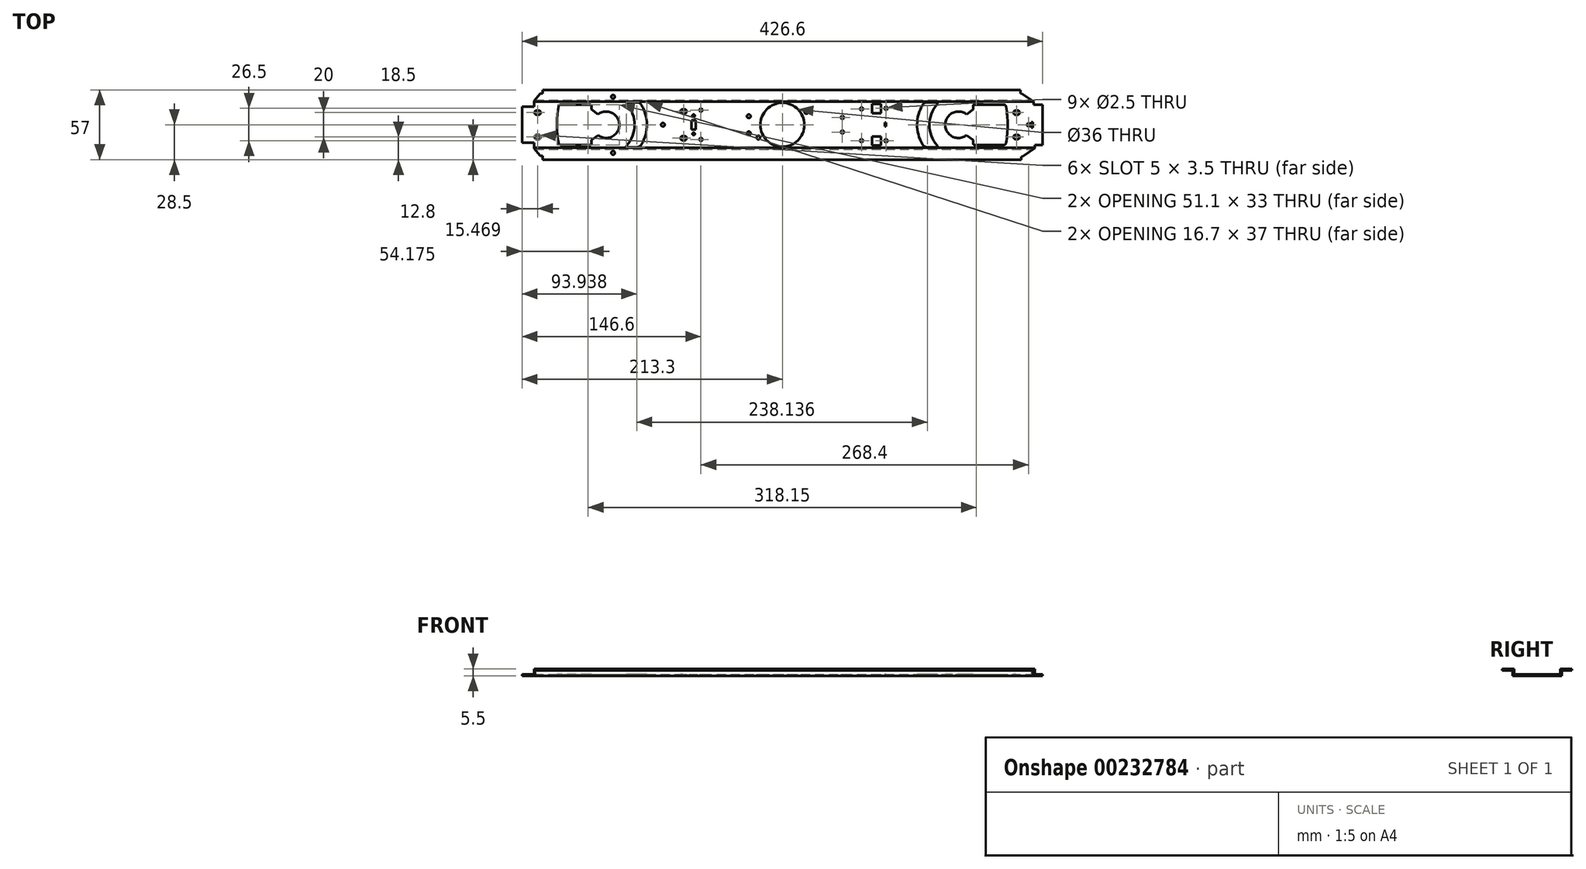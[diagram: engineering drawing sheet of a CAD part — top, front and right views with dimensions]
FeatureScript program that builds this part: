
annotation { "Feature Type Name" : "Feature", "Feature Type Description" : "" }
export const myFeature = defineFeature(function(context is Context, id is Id, definition is map)
    precondition{}
    {
        {
            var Q0;
            Q0=qCreatedBy(makeId("Top.planeOp"),FACE);
            var sketch = newSketch(context, id + "F0", { "sketchPlane" : qUnion([Q0])});
            skLineSegment(sketch, "E0.bottom", {"start": v(193, 29.4) * mm, "end": v(-197, 29.4) * mm});
            skLineSegment(sketch, "E0.top", {"start": v(193, -29.1) * mm, "end": v(-197, -29.1) * mm});
            skLineSegment(sketch, "E0.left", {"start": v(193, 29.4) * mm, "end": v(193, 26.65) * mm});
            skLineSegment(sketch, "E0.right", {"start": v(-197, 29.4) * mm, "end": v(-197, 26.8) * mm});
            skLineSegment(sketch, "E1.bottom", {"start": v(204, 19) * mm, "end": v(-204, 19) * mm, "construction": true});
            skLineSegment(sketch, "E1.top", {"start": v(204, -19) * mm, "end": v(-204, -19) * mm, "construction": true});
            skLineSegment(sketch, "E1.left", {"start": v(204, 19) * mm, "end": v(204, 17.25) * mm});
            skLineSegment(sketch, "E1.right", {"start": v(-204, 19) * mm, "end": v(-204, 15.75) * mm});
            skPoint(sketch, "E1.middle", {"position": v(0, 0) * mm});
            skPoint(sketch, "E2", {"position": v(193, 26.65) * mm});
            skPoint(sketch, "E3", {"position": v(194.1, 26.65) * mm});
            skLineSegment(sketch, "E4", {"start": v(194.1, 26.65) * mm, "end": v(204, 19) * mm});
            skLineSegment(sketch, "E5", {"start": v(194.1, 26.65) * mm, "end": v(193, 26.65) * mm});
            skLineSegment(sketch, "E6.MirrorCS", {"start": v(194.1, -26.65) * mm, "end": v(204, -19) * mm});
            skLineSegment(sketch, "E7.MirrorCS", {"start": v(194.1, -26.65) * mm, "end": v(193, -26.65) * mm});
            skPoint(sketch, "E8", {"position": v(-197, 26.8) * mm});
            skPoint(sketch, "E9", {"position": v(-199, 26.8) * mm});
            skLineSegment(sketch, "E10", {"start": v(-199, 26.8) * mm, "end": v(-204, 19) * mm});
            skLineSegment(sketch, "E11", {"start": v(-199, 26.8) * mm, "end": v(-197, 26.8) * mm});
            skLineSegment(sketch, "E12.MirrorCS", {"start": v(-199, -26.8) * mm, "end": v(-197, -26.8) * mm});
            skLineSegment(sketch, "E13.MirrorCS", {"start": v(-199, -26.8) * mm, "end": v(-204, -19) * mm});
            skPoint(sketch, "E14", {"position": v(-204, 0) * mm});
            skLineSegment(sketch, "E15", {"start": v(210.5, 0) * mm, "end": v(-236.37, 0) * mm, "construction": true});
            skPoint(sketch, "E16", {"position": v(-204, 29.4) * mm});
            skLineSegment(sketch, "E17", {"start": v(-204, -15.75) * mm, "end": v(-204, -19) * mm});
            skLineSegment(sketch, "E18", {"start": v(-204, 15.75) * mm, "end": v(-214.3, 15.75) * mm});
            skLineSegment(sketch, "E19", {"start": v(-214.3, 15.75) * mm, "end": v(-214.3, -15.75) * mm});
            skLineSegment(sketch, "E20", {"start": v(-214.3, -15.75) * mm, "end": v(-204, -15.75) * mm});
            skLineSegment(sketch, "E21", {"start": v(204, 17.25) * mm, "end": v(204, -17.25) * mm, "construction": true});
            skLineSegment(sketch, "E22", {"start": v(204, -17.25) * mm, "end": v(204, -19) * mm});
            skLineSegment(sketch, "E23", {"start": v(204, 17.25) * mm, "end": v(210.5, 17.25) * mm});
            skLineSegment(sketch, "E24", {"start": v(210.5, 17.25) * mm, "end": v(210.5, -17.25) * mm});
            skLineSegment(sketch, "E25", {"start": v(210.5, -17.25) * mm, "end": v(204, -17.25) * mm});
            skLineSegment(sketch, "E26", {"start": v(-197, 26.8) * mm, "end": v(-197, -26.8) * mm, "construction": true});
            skLineSegment(sketch, "E27", {"start": v(-197, -26.8) * mm, "end": v(-197, -29.1) * mm});
            skLineSegment(sketch, "E28", {"start": v(193, -26.65) * mm, "end": v(193, -29.1) * mm});
            skLineSegment(sketch, "E29", {"start": v(193, 26.65) * mm, "end": v(193, -26.65) * mm, "construction": true});
            skSolve(sketch);
        }
        {
            var Q0;
            Q0=qCreatedBy(makeId("Right.planeOp"),FACE);
            var sketch = newSketch(context, id + "F1", { "sketchPlane" : qUnion([Q0])});
            skLineSegment(sketch, "E30", {"start": v(0, 0) * mm, "end": v(20.1, 0) * mm});
            skPoint(sketch, "E31", {"position": v(20.1, 0) * mm});
            skLineSegment(sketch, "E32", {"start": v(20.1, 0) * mm, "end": v(20.1, 4.25) * mm});
            skPoint(sketch, "E33", {"position": v(29.4, 0) * mm});
            skLineSegment(sketch, "E34", {"start": v(20.1, 4.25) * mm, "end": v(29.4, 4.25) * mm});
            skLineSegment(sketch, "E35.0", {"start": v(18.85, 5.5) * mm, "end": v(29.4, 5.5) * mm});
            skLineSegment(sketch, "E35.1", {"start": v(18.85, 1.25) * mm, "end": v(18.85, 5.5) * mm});
            skLineSegment(sketch, "E35.2", {"start": v(0, 1.25) * mm, "end": v(18.85, 1.25) * mm});
            skLineSegment(sketch, "E36", {"start": v(29.4, 5.5) * mm, "end": v(29.4, 4.25) * mm});
            skLineSegment(sketch, "E37.MirrorCS", {"start": v(-29.4, 5.5) * mm, "end": v(-29.4, 4.25) * mm});
            skLineSegment(sketch, "E38.MirrorCS", {"start": v(0, 0) * mm, "end": v(-20.1, 0) * mm});
            skLineSegment(sketch, "E39.MirrorCS", {"start": v(0, 1.25) * mm, "end": v(-18.85, 1.25) * mm});
            skLineSegment(sketch, "E40.MirrorCS", {"start": v(-18.85, 1.25) * mm, "end": v(-18.85, 5.5) * mm});
            skLineSegment(sketch, "E41.MirrorCS", {"start": v(-20.1, 0) * mm, "end": v(-20.1, 4.25) * mm});
            skLineSegment(sketch, "E42.MirrorCS", {"start": v(-18.85, 5.5) * mm, "end": v(-29.4, 5.5) * mm});
            skLineSegment(sketch, "E43.MirrorCS", {"start": v(-20.1, 4.25) * mm, "end": v(-29.4, 4.25) * mm});
            skSolve(sketch);
        }
        {
            var Q0;
            Q0=makeQuery(id+"F1.imprint","IMPRINT",FACE,{"disambiguationData":[TD([[makeQuery(id+"F1.imprint","IMPRINT",EDGE,{"derivedFrom":sQuery(id+"F1.wireOp",EDGE,"E30")}),1.0]])]});
            extrude(context, id + "F2", {"entities" : qUnion([Q0]), "oppositeDirection" : true, "depth" : 213.75 * mm, "hasSecondDirection" : true, "secondDirectionOppositeDirection" : false, "secondDirectionDepth" : 213.3 * mm});
        }
        {
            var Q0;
            Q0=qCreatedBy(makeId("Top.planeOp"),FACE);
            var sketch = newSketch(context, id + "F3", { "sketchPlane" : qUnion([Q0])});
            skCircle(sketch, "E44", {"center": v(-27.5, 7) * mm, "radius": 1.5 * mm});
            skCircle(sketch, "E45", {"center": v(-66.7, 12) * mm, "radius": 1.25 * mm});
            skCircle(sketch, "E46", {"center": v(-97.9, 0) * mm, "radius": 1.5 * mm});
            skCircle(sketch, "E47", {"center": v(-72.7, 7.5) * mm, "radius": 1 * mm});
            skPoint(sketch, "E48", {"position": v(-200.5, 10) * mm});
            skLineSegment(sketch, "E49.bottom", {"start": v(-199.75, 11.75) * mm, "end": v(-201.25, 11.75) * mm});
            skLineSegment(sketch, "E49.top", {"start": v(-199.75, 8.25) * mm, "end": v(-201.25, 8.25) * mm});
            skLineSegment(sketch, "E49.left", {"start": v(-196.26, 9.62) * mm, "end": v(-196.26, 9.62) * mm});
            skLineSegment(sketch, "E49.right", {"start": v(-201.26, 9.62) * mm, "end": v(-201.26, 9.62) * mm});
            skPoint(sketch, "E50.visualSharp", {"position": v(-203, 11.75) * mm});
            skArc(sketch, "E50.filletArc", {"start": v(-201.25, 11.75) * mm, "mid": v(-202.49, 11.24) * mm, "end": v(-203, 10) * mm});
            skPoint(sketch, "E51.visualSharp", {"position": v(-203, 8.25) * mm});
            skArc(sketch, "E51.filletArc", {"start": v(-203, 10) * mm, "mid": v(-202.49, 8.76) * mm, "end": v(-201.25, 8.25) * mm});
            skPoint(sketch, "E52.visualSharp", {"position": v(-198, 8.25) * mm});
            skArc(sketch, "E52.filletArc", {"start": v(-199.75, 8.25) * mm, "mid": v(-198.51, 8.76) * mm, "end": v(-198, 10) * mm});
            skPoint(sketch, "E53.visualSharp", {"position": v(-198, 11.75) * mm});
            skArc(sketch, "E53.filletArc", {"start": v(-198, 10) * mm, "mid": v(-198.51, 11.24) * mm, "end": v(-199.75, 11.75) * mm});
            skPoint(sketch, "E54", {"position": v(77.2, 13.25) * mm});
            skLineSegment(sketch, "E55.bottom", {"start": v(80.95, 9.5) * mm, "end": v(73.45, 9.5) * mm});
            skLineSegment(sketch, "E55.top", {"start": v(80.95, 17) * mm, "end": v(73.45, 17) * mm});
            skLineSegment(sketch, "E55.left", {"start": v(80.95, 9.5) * mm, "end": v(80.95, 17) * mm});
            skLineSegment(sketch, "E55.right", {"start": v(73.45, 9.5) * mm, "end": v(73.45, 17) * mm});
            skPoint(sketch, "E56", {"position": v(84.95, 13.47) * mm});
            skCircle(sketch, "E57", {"center": v(84.95, 13.47) * mm, "radius": 1.25 * mm});
            skPoint(sketch, "E58", {"position": v(64.9, 13) * mm});
            skCircle(sketch, "E59", {"center": v(64.9, 13) * mm, "radius": 1.25 * mm});
            skPoint(sketch, "E60", {"position": v(49.2, 6) * mm});
            skCircle(sketch, "E61", {"center": v(49.2, 6) * mm, "radius": 1.25 * mm});
            skPoint(sketch, "E62", {"position": v(-78.4, 12.75) * mm});
            skPoint(sketch, "E63", {"position": v(-80.9, 11) * mm});
            skLineSegment(sketch, "E64.bottom", {"start": v(-80.15, 12.75) * mm, "end": v(-81.65, 12.75) * mm});
            skLineSegment(sketch, "E64.top", {"start": v(-80.15, 9.25) * mm, "end": v(-81.65, 9.25) * mm});
            skLineSegment(sketch, "E64.left", {"start": v(-77.26, 10.62) * mm, "end": v(-77.26, 10.62) * mm});
            skLineSegment(sketch, "E64.right", {"start": v(-82.26, 10.62) * mm, "end": v(-82.26, 10.62) * mm});
            skPoint(sketch, "E65.visualSharp", {"position": v(-83.4, 12.75) * mm});
            skArc(sketch, "E65.filletArc", {"start": v(-81.65, 12.75) * mm, "mid": v(-82.89, 12.24) * mm, "end": v(-83.4, 11) * mm});
            skPoint(sketch, "E66.visualSharp", {"position": v(-83.4, 9.25) * mm});
            skArc(sketch, "E66.filletArc", {"start": v(-83.4, 11) * mm, "mid": v(-82.89, 9.76) * mm, "end": v(-81.65, 9.25) * mm});
            skPoint(sketch, "E67.visualSharp", {"position": v(-78.4, 9.25) * mm});
            skArc(sketch, "E67.filletArc", {"start": v(-80.15, 9.25) * mm, "mid": v(-78.91, 9.76) * mm, "end": v(-78.4, 11) * mm});
            skArc(sketch, "E68.filletArc", {"start": v(-78.4, 11) * mm, "mid": v(-78.91, 12.24) * mm, "end": v(-80.15, 12.75) * mm});
            skPoint(sketch, "E69", {"position": v(204.7, 0) * mm});
            skLineSegment(sketch, "E70.bottom", {"start": v(205.4, 2.25) * mm, "end": v(204, 2.25) * mm});
            skLineSegment(sketch, "E70.top", {"start": v(205.4, -2.25) * mm, "end": v(204, -2.25) * mm});
            skLineSegment(sketch, "E70.left", {"start": v(205.4, 2.25) * mm, "end": v(205.4, -2.25) * mm});
            skLineSegment(sketch, "E70.right", {"start": v(204, 2.25) * mm, "end": v(204, -2.25) * mm});
            skCircle(sketch, "E71", {"center": v(201.7, 0) * mm, "radius": 1.25 * mm});
            skCircle(sketch, "E72", {"center": v(0, 0) * mm, "radius": 18 * mm});
            skPoint(sketch, "E73", {"position": v(185.38, 0) * mm});
            skLineSegment(sketch, "E74", {"start": v(158.01, 16.5) * mm, "end": v(181.48, 16.5) * mm});
            skPoint(sketch, "E75", {"position": v(183.34, 14.81) * mm});
            skArc(sketch, "E76", {"start": v(184.58, 0) * mm, "mid": v(184.27, 7.43) * mm, "end": v(183.34, 14.81) * mm});
            skArc(sketch, "E77", {"start": v(183.34, 14.81) * mm, "mid": v(182.71, 15.99) * mm, "end": v(181.48, 16.5) * mm});
            skArc(sketch, "E78", {"start": v(150.98, 8.51) * mm, "mid": v(133.48, 0) * mm, "end": v(150.98, -8.51) * mm});
            skLineSegment(sketch, "E79.left", {"start": v(195, 28.5) * mm, "end": v(195, 25.75) * mm});
            skLineSegment(sketch, "E79.right", {"start": v(-196.3, 28.5) * mm, "end": v(-196.3, 25.5) * mm});
            skLineSegment(sketch, "E80.left", {"start": v(206, 18.85) * mm, "end": v(206, 16.35) * mm});
            skLineSegment(sketch, "E80.right", {"start": v(-203.3, 19.5) * mm, "end": v(-203.3, 14.7) * mm});
            skLineSegment(sketch, "E81", {"start": v(196, 25.75) * mm, "end": v(195, 25.75) * mm});
            skLineSegment(sketch, "E82", {"start": v(-203.3, 14.7) * mm, "end": v(-212.3, 14.7) * mm});
            skLineSegment(sketch, "E83.bottom", {"start": v(-70.95, 3.75) * mm, "end": v(-74.45, 3.75) * mm});
            skLineSegment(sketch, "E83.top", {"start": v(-70.95, -3.75) * mm, "end": v(-74.45, -3.75) * mm});
            skLineSegment(sketch, "E83.left", {"start": v(-70.95, 3.75) * mm, "end": v(-70.95, -3.75) * mm});
            skLineSegment(sketch, "E83.right", {"start": v(-74.45, 3.75) * mm, "end": v(-74.45, -3.75) * mm});
            skPoint(sketch, "E83.middle", {"position": v(-72.7, 0) * mm});
            skLineSegment(sketch, "E84", {"start": v(0, 0) * mm, "end": v(-259.12, 0) * mm, "construction": true});
            skLineSegment(sketch, "E85", {"start": v(0, 0) * mm, "end": v(296.57, 0) * mm, "construction": true});
            skPoint(sketch, "E86", {"position": v(-144.4, 0) * mm});
            skPoint(sketch, "E87", {"position": v(194.4, 11.75) * mm});
            skPoint(sketch, "E88", {"position": v(191.9, 10) * mm});
            skLineSegment(sketch, "E89.bottom", {"start": v(192.65, 11.75) * mm, "end": v(191.15, 11.75) * mm});
            skLineSegment(sketch, "E89.top", {"start": v(192.65, 8.25) * mm, "end": v(191.15, 8.25) * mm});
            skLineSegment(sketch, "E89.left", {"start": v(196.6, 16.48) * mm, "end": v(196.6, 16.48) * mm});
            skLineSegment(sketch, "E89.right", {"start": v(191.6, 16.48) * mm, "end": v(191.6, 16.48) * mm});
            skPoint(sketch, "E90.visualSharp", {"position": v(189.4, 11.75) * mm});
            skArc(sketch, "E90.filletArc", {"start": v(191.15, 11.75) * mm, "mid": v(189.91, 11.24) * mm, "end": v(189.4, 10) * mm});
            skPoint(sketch, "E91.visualSharp", {"position": v(189.4, 8.25) * mm});
            skArc(sketch, "E91.filletArc", {"start": v(189.4, 10) * mm, "mid": v(189.91, 8.76) * mm, "end": v(191.15, 8.25) * mm});
            skPoint(sketch, "E92.visualSharp", {"position": v(194.4, 8.25) * mm});
            skArc(sketch, "E92.filletArc", {"start": v(192.65, 8.25) * mm, "mid": v(193.89, 8.76) * mm, "end": v(194.4, 10) * mm});
            skArc(sketch, "E93.filletArc", {"start": v(194.4, 10) * mm, "mid": v(193.89, 11.24) * mm, "end": v(192.65, 11.75) * mm});
            skArc(sketch, "E94.MirrorCS", {"start": v(-199.75, -8.25) * mm, "mid": v(-198.51, -8.76) * mm, "end": v(-198, -10) * mm});
            skArc(sketch, "E95.MirrorCS", {"start": v(-198, -10) * mm, "mid": v(-198.51, -11.24) * mm, "end": v(-199.75, -11.75) * mm});
            skLineSegment(sketch, "E96.MirrorCS", {"start": v(-199.75, -11.75) * mm, "end": v(-201.25, -11.75) * mm});
            skPoint(sketch, "E97.MirrorP", {"position": v(-200.5, -10) * mm});
            skPoint(sketch, "E98.MirrorP", {"position": v(-198, -11.75) * mm});
            skArc(sketch, "E99.MirrorCS", {"start": v(-201.25, -11.75) * mm, "mid": v(-202.49, -11.24) * mm, "end": v(-203, -10) * mm});
            skPoint(sketch, "E100.MirrorP", {"position": v(-203, -11.75) * mm});
            skArc(sketch, "E101.MirrorCS", {"start": v(-203, -10) * mm, "mid": v(-202.49, -8.76) * mm, "end": v(-201.25, -8.25) * mm});
            skPoint(sketch, "E102.MirrorP", {"position": v(-198, -8.25) * mm});
            skLineSegment(sketch, "E103.MirrorCS", {"start": v(-199.75, -8.25) * mm, "end": v(-201.25, -8.25) * mm});
            skPoint(sketch, "E104.MirrorP", {"position": v(-203, -8.25) * mm});
            skArc(sketch, "E105.MirrorCS", {"start": v(-78.4, -11) * mm, "mid": v(-78.91, -12.24) * mm, "end": v(-80.15, -12.75) * mm});
            skLineSegment(sketch, "E106.MirrorCS", {"start": v(-80.15, -12.75) * mm, "end": v(-81.65, -12.75) * mm});
            skArc(sketch, "E107.MirrorCS", {"start": v(-81.65, -12.75) * mm, "mid": v(-82.89, -12.24) * mm, "end": v(-83.4, -11) * mm});
            skLineSegment(sketch, "E108.MirrorCS", {"start": v(-80.15, -9.25) * mm, "end": v(-81.65, -9.25) * mm});
            skArc(sketch, "E109.MirrorCS", {"start": v(-80.15, -9.25) * mm, "mid": v(-78.91, -9.76) * mm, "end": v(-78.4, -11) * mm});
            skArc(sketch, "E110.MirrorCS", {"start": v(-83.4, -11) * mm, "mid": v(-82.89, -9.76) * mm, "end": v(-81.65, -9.25) * mm});
            skPoint(sketch, "E111.MirrorP", {"position": v(-80.9, -11) * mm});
            skPoint(sketch, "E112.MirrorP", {"position": v(-78.4, -12.75) * mm});
            skCircle(sketch, "E113.MirrorC", {"center": v(-72.7, -7.5) * mm, "radius": 1 * mm});
            skCircle(sketch, "E114.MirrorC", {"center": v(-66.7, -12) * mm, "radius": 1.25 * mm});
            skPoint(sketch, "E115.MirrorP", {"position": v(-83.4, -12.75) * mm});
            skPoint(sketch, "E116.MirrorP", {"position": v(-83.4, -9.25) * mm});
            skPoint(sketch, "E117.MirrorP", {"position": v(-78.4, -9.25) * mm});
            skLineSegment(sketch, "E118.MirrorCS", {"start": v(80.95, -9.5) * mm, "end": v(80.95, -17) * mm});
            skCircle(sketch, "E119.MirrorC", {"center": v(49.2, -6) * mm, "radius": 1.25 * mm});
            skCircle(sketch, "E120.MirrorC", {"center": v(84.95, -13.03) * mm, "radius": 1.25 * mm});
            skCircle(sketch, "E121.MirrorC", {"center": v(64.9, -13) * mm, "radius": 1.25 * mm});
            skPoint(sketch, "E122.MirrorP", {"position": v(77.2, -13.25) * mm});
            skLineSegment(sketch, "E123.MirrorCS", {"start": v(73.45, -9.5) * mm, "end": v(73.45, -17) * mm});
            skLineSegment(sketch, "E124.MirrorCS", {"start": v(80.95, -9.5) * mm, "end": v(73.45, -9.5) * mm});
            skLineSegment(sketch, "E125.MirrorCS", {"start": v(80.95, -17) * mm, "end": v(73.45, -17) * mm});
            skPoint(sketch, "E126.MirrorP", {"position": v(191.9, -10) * mm});
            skPoint(sketch, "E127.MirrorP", {"position": v(194.4, -11.75) * mm});
            skPoint(sketch, "E128.MirrorP", {"position": v(189.4, -8.25) * mm});
            skPoint(sketch, "E129.MirrorP", {"position": v(194.4, -8.25) * mm});
            skArc(sketch, "E130.MirrorCS", {"start": v(194.4, -10) * mm, "mid": v(193.89, -11.24) * mm, "end": v(192.65, -11.75) * mm});
            skPoint(sketch, "E131.MirrorP", {"position": v(189.4, -11.75) * mm});
            skArc(sketch, "E132.MirrorCS", {"start": v(192.65, -8.25) * mm, "mid": v(193.89, -8.76) * mm, "end": v(194.4, -10) * mm});
            skLineSegment(sketch, "E133.MirrorCS", {"start": v(192.65, -11.75) * mm, "end": v(191.15, -11.75) * mm});
            skLineSegment(sketch, "E134.MirrorCS", {"start": v(192.65, -8.25) * mm, "end": v(191.15, -8.25) * mm});
            skArc(sketch, "E135.MirrorCS", {"start": v(189.4, -10) * mm, "mid": v(189.91, -8.76) * mm, "end": v(191.15, -8.25) * mm});
            skArc(sketch, "E136.MirrorCS", {"start": v(191.15, -11.75) * mm, "mid": v(189.91, -11.24) * mm, "end": v(189.4, -10) * mm});
            skPoint(sketch, "E137.middle", {"position": v(123.91, 0) * mm});
            skArc(sketch, "E138", {"start": v(126.77, 16.8) * mm, "mid": v(120.41, -0.1) * mm, "end": v(126.9, -16.95) * mm});
            skPoint(sketch, "E139", {"position": v(116.41, 18.5) * mm});
            skArc(sketch, "E140", {"start": v(115.02, 16.41) * mm, "mid": v(110.42, 0.3) * mm, "end": v(114.71, -15.89) * mm});
            skLineSegment(sketch, "E141", {"start": v(126.2, -18.5) * mm, "end": v(119.26, -18.5) * mm});
            skLineSegment(sketch, "E142", {"start": v(118.74, 18.5) * mm, "end": v(126, 18.5) * mm});
            skPoint(sketch, "E143.visualSharp", {"position": v(128.41, 18.5) * mm});
            skArc(sketch, "E143.filletArc", {"start": v(126.77, 16.8) * mm, "mid": v(126.94, 17.9) * mm, "end": v(126, 18.5) * mm});
            skArc(sketch, "E144.filletArc", {"start": v(118.74, 18.5) * mm, "mid": v(116.6, 17.94) * mm, "end": v(115.02, 16.41) * mm});
            skPoint(sketch, "E145.visualSharp", {"position": v(128.41, -18.5) * mm});
            skArc(sketch, "E145.filletArc", {"start": v(126.2, -18.5) * mm, "mid": v(127.05, -17.95) * mm, "end": v(126.9, -16.95) * mm});
            skPoint(sketch, "E146.visualSharp", {"position": v(116.41, -18.5) * mm});
            skArc(sketch, "E146.filletArc", {"start": v(114.71, -15.89) * mm, "mid": v(116.64, -17.8) * mm, "end": v(119.26, -18.5) * mm});
            skLineSegment(sketch, "E147", {"start": v(196, 25.75) * mm, "end": v(206, 18.85) * mm});
            skPoint(sketch, "E148", {"position": v(-195.3, 28.5) * mm});
            skLineSegment(sketch, "E149", {"start": v(-196.3, 25.5) * mm, "end": v(-198.3, 25.5) * mm});
            skLineSegment(sketch, "E150", {"start": v(-198.3, 25.5) * mm, "end": v(-203.3, 19.5) * mm});
            skLineSegment(sketch, "E151", {"start": v(194.5, 28.5) * mm, "end": v(-195.3, 28.5) * mm});
            skPoint(sketch, "E152", {"position": v(-114.44, 28.5) * mm});
            skPoint(sketch, "E153", {"position": v(212.75, 18.12) * mm});
            skLineSegment(sketch, "E154.MirrorCS", {"start": v(196.75, -26) * mm, "end": v(195.75, -26) * mm});
            skLineSegment(sketch, "E155.MirrorCS", {"start": v(206.75, -19.1) * mm, "end": v(206.75, -16.6) * mm});
            skLineSegment(sketch, "E156.MirrorCS", {"start": v(196.75, -26) * mm, "end": v(206.75, -19.1) * mm});
            skLineSegment(sketch, "E157.MirrorCS", {"start": v(195.75, -28.5) * mm, "end": v(195.75, -26) * mm});
            skLineSegment(sketch, "E158.MirrorCS", {"start": v(195.75, -28.5) * mm, "end": v(-194.8, -28.5) * mm});
            skLineSegment(sketch, "E159.MirrorCS", {"start": v(-196.3, -28.5) * mm, "end": v(-196.3, -25.5) * mm});
            skLineSegment(sketch, "E160.MirrorCS", {"start": v(-196.3, -25.5) * mm, "end": v(-198.3, -25.5) * mm});
            skLineSegment(sketch, "E161.MirrorCS", {"start": v(-203.3, -14.7) * mm, "end": v(-212.3, -14.7) * mm});
            skLineSegment(sketch, "E162.MirrorCS", {"start": v(-198.3, -25.5) * mm, "end": v(-203.3, -19.5) * mm});
            skLineSegment(sketch, "E163.MirrorCS", {"start": v(-203.3, -19.5) * mm, "end": v(-203.3, -14.7) * mm});
            skPoint(sketch, "E164.MirrorP", {"position": v(-195.3, -28.5) * mm});
            skLineSegment(sketch, "E165", {"start": v(-213.3, 14.7) * mm, "end": v(-213.3, -14.7) * mm});
            skLineSegment(sketch, "E166", {"start": v(213.75, 45.34) * mm, "end": v(213.75, -40.98) * mm, "construction": true});
            skLineSegment(sketch, "E167", {"start": v(206.25, 44.05) * mm, "end": v(206.25, -40.86) * mm, "construction": true});
            skLineSegment(sketch, "E168", {"start": v(195.25, 35.34) * mm, "end": v(195.25, -39.06) * mm, "construction": true});
            skLineSegment(sketch, "E169", {"start": v(206, 16.35) * mm, "end": v(213.75, 16.35) * mm});
            skLineSegment(sketch, "E170", {"start": v(213.75, 16.35) * mm, "end": v(213.75, -16.6) * mm});
            skLineSegment(sketch, "E171", {"start": v(213.75, -16.6) * mm, "end": v(206.75, -16.6) * mm});
            skPoint(sketch, "E172", {"position": v(-229.5, -17.54) * mm});
            skLineSegment(sketch, "E173", {"start": v(-202, 48.4) * mm, "end": v(-202, -44.33) * mm, "construction": true});
            skLineSegment(sketch, "E174", {"start": v(-195.5, 51.08) * mm, "end": v(-195.5, -42.68) * mm, "construction": true});
            skArc(sketch, "E175.MirrorCS", {"start": v(-126.79, -18.5) * mm, "mid": v(-127.64, -17.95) * mm, "end": v(-127.48, -16.95) * mm});
            skArc(sketch, "E176.MirrorCS", {"start": v(-119.33, 18.5) * mm, "mid": v(-117.2, 17.94) * mm, "end": v(-115.61, 16.41) * mm});
            skArc(sketch, "E177.MirrorCS", {"start": v(-115.3, -15.89) * mm, "mid": v(-117.22, -17.8) * mm, "end": v(-119.84, -18.5) * mm});
            skArc(sketch, "E178.MirrorCS", {"start": v(-127.36, 16.8) * mm, "mid": v(-127.52, 17.9) * mm, "end": v(-126.6, 18.5) * mm});
            skPoint(sketch, "E179.MirrorP", {"position": v(-117, 18.5) * mm});
            skLineSegment(sketch, "E180.MirrorCS", {"start": v(-126.79, -18.5) * mm, "end": v(-119.84, -18.5) * mm});
            skLineSegment(sketch, "E181.MirrorCS", {"start": v(-119.33, 18.5) * mm, "end": v(-126.6, 18.5) * mm});
            skPoint(sketch, "E182.MirrorP", {"position": v(-129, -18.5) * mm});
            skArc(sketch, "E183.MirrorCS", {"start": v(-115.61, 16.41) * mm, "mid": v(-111.01, 0.3) * mm, "end": v(-115.3, -15.89) * mm});
            skArc(sketch, "E184.MirrorCS", {"start": v(-127.36, 16.8) * mm, "mid": v(-121, -0.1) * mm, "end": v(-127.48, -16.95) * mm});
            skPoint(sketch, "E185.MirrorP", {"position": v(-129, 18.5) * mm});
            skPoint(sketch, "E186.MirrorP", {"position": v(-117, -18.5) * mm});
            skPoint(sketch, "E187.MirrorP", {"position": v(-125, 0) * mm});
            skCircle(sketch, "E188.MirrorC", {"center": v(-27.5, -7) * mm, "radius": 1.5 * mm});
            skLineSegment(sketch, "E189", {"start": v(194.5, 28.5) * mm, "end": v(195, 28.5) * mm});
            skLineSegment(sketch, "E190", {"start": v(-195.3, 28.5) * mm, "end": v(-196.3, 28.5) * mm});
            skLineSegment(sketch, "E191", {"start": v(-194.8, -28.5) * mm, "end": v(-196.3, -28.5) * mm});
            skLineSegment(sketch, "E192", {"start": v(-212.3, 14.7) * mm, "end": v(-213.3, 14.7) * mm});
            skLineSegment(sketch, "E193", {"start": v(-212.3, -14.7) * mm, "end": v(-213.3, -14.7) * mm});
            skPoint(sketch, "E194", {"position": v(150.98, 8.51) * mm});
            skPoint(sketch, "E195", {"position": v(156.28, 12.48) * mm});
            skLineSegment(sketch, "E196", {"start": v(150.98, 8.51) * mm, "end": v(156.28, 12.48) * mm});
            skLineSegment(sketch, "E197", {"start": v(156.28, 15.46) * mm, "end": v(156.28, 12.48) * mm});
            skLineSegment(sketch, "E198", {"start": v(158.01, 16.5) * mm, "end": v(157.37, 16.5) * mm});
            skArc(sketch, "E199", {"start": v(157.37, 16.5) * mm, "mid": v(156.62, 16.19) * mm, "end": v(156.28, 15.46) * mm});
            skPoint(sketch, "E200.start.orphan", {"position": v(156.28, 16.5) * mm});
            skPoint(sketch, "E201.orphan", {"position": v(156.28, 15.74) * mm});
            skLineSegment(sketch, "E202.MirrorCS", {"start": v(158.01, -16.5) * mm, "end": v(157.37, -16.5) * mm});
            skArc(sketch, "E203.MirrorCS", {"start": v(157.37, -16.5) * mm, "mid": v(156.62, -16.19) * mm, "end": v(156.28, -15.46) * mm});
            skPoint(sketch, "E204.MirrorP", {"position": v(156.28, -15.74) * mm});
            skPoint(sketch, "E205.MirrorP", {"position": v(156.28, -12.48) * mm});
            skPoint(sketch, "E206.MirrorP", {"position": v(150.98, -8.51) * mm});
            skArc(sketch, "E207.MirrorCS", {"start": v(184.58, 0) * mm, "mid": v(184.27, -7.43) * mm, "end": v(183.34, -14.81) * mm});
            skPoint(sketch, "E208.MirrorP", {"position": v(156.28, -16.5) * mm});
            skLineSegment(sketch, "E209.MirrorCS", {"start": v(158.01, -16.5) * mm, "end": v(181.48, -16.5) * mm});
            skPoint(sketch, "E210.MirrorP", {"position": v(183.34, -14.81) * mm});
            skLineSegment(sketch, "E211.MirrorCS", {"start": v(150.98, -8.51) * mm, "end": v(156.28, -12.48) * mm});
            skLineSegment(sketch, "E212.MirrorCS", {"start": v(156.28, -15.46) * mm, "end": v(156.28, -12.48) * mm});
            skArc(sketch, "E213.MirrorCS", {"start": v(183.34, -14.81) * mm, "mid": v(182.71, -15.99) * mm, "end": v(181.48, -16.5) * mm});
            skPoint(sketch, "E214", {"position": v(-185.48, 0) * mm});
            skLineSegment(sketch, "E215", {"start": v(-158.11, -16.5) * mm, "end": v(-181.58, -16.5) * mm});
            skPoint(sketch, "E216", {"position": v(-183.44, -14.81) * mm});
            skArc(sketch, "E217", {"start": v(-184.68, 0) * mm, "mid": v(-184.37, -7.43) * mm, "end": v(-183.44, -14.81) * mm});
            skArc(sketch, "E218", {"start": v(-183.44, -14.81) * mm, "mid": v(-182.81, -15.99) * mm, "end": v(-181.58, -16.5) * mm});
            skArc(sketch, "E219", {"start": v(-151.08, -8.51) * mm, "mid": v(-133.58, 0) * mm, "end": v(-151.08, 8.51) * mm});
            skPoint(sketch, "E220", {"position": v(-151.08, -8.51) * mm});
            skPoint(sketch, "E221", {"position": v(-156.38, -12.48) * mm});
            skLineSegment(sketch, "E222", {"start": v(-151.08, -8.51) * mm, "end": v(-156.38, -12.48) * mm});
            skLineSegment(sketch, "E223", {"start": v(-156.38, -15.46) * mm, "end": v(-156.38, -12.48) * mm});
            skLineSegment(sketch, "E224", {"start": v(-158.11, -16.5) * mm, "end": v(-157.47, -16.5) * mm});
            skArc(sketch, "E225", {"start": v(-157.47, -16.5) * mm, "mid": v(-156.72, -16.19) * mm, "end": v(-156.38, -15.46) * mm});
            skPoint(sketch, "E226.start.orphan", {"position": v(-156.38, -16.5) * mm});
            skPoint(sketch, "E227.orphan", {"position": v(-156.38, -15.74) * mm});
            skLineSegment(sketch, "E228.MirrorCS", {"start": v(-158.11, 16.5) * mm, "end": v(-157.47, 16.5) * mm});
            skArc(sketch, "E229.MirrorCS", {"start": v(-157.47, 16.5) * mm, "mid": v(-156.72, 16.19) * mm, "end": v(-156.38, 15.46) * mm});
            skPoint(sketch, "E230.MirrorP", {"position": v(-156.38, 15.74) * mm});
            skPoint(sketch, "E231.MirrorP", {"position": v(-156.38, 12.48) * mm});
            skPoint(sketch, "E232.MirrorP", {"position": v(-151.08, 8.51) * mm});
            skArc(sketch, "E233.MirrorCS", {"start": v(-184.68, 0) * mm, "mid": v(-184.37, 7.43) * mm, "end": v(-183.44, 14.81) * mm});
            skPoint(sketch, "E234.MirrorP", {"position": v(-156.38, 16.5) * mm});
            skLineSegment(sketch, "E235.MirrorCS", {"start": v(-158.11, 16.5) * mm, "end": v(-181.58, 16.5) * mm});
            skPoint(sketch, "E236.MirrorP", {"position": v(-183.44, 14.81) * mm});
            skLineSegment(sketch, "E237.MirrorCS", {"start": v(-151.08, 8.51) * mm, "end": v(-156.38, 12.48) * mm});
            skLineSegment(sketch, "E238.MirrorCS", {"start": v(-156.38, 15.46) * mm, "end": v(-156.38, 12.48) * mm});
            skArc(sketch, "E239.MirrorCS", {"start": v(-183.44, 14.81) * mm, "mid": v(-182.81, 15.99) * mm, "end": v(-181.58, 16.5) * mm});
            skCircle(sketch, "E240", {"center": v(-138.7, 23) * mm, "radius": 1.5 * mm});
            skCircle(sketch, "E241.MirrorC", {"center": v(-138.7, -23) * mm, "radius": 1.5 * mm});
            skLineSegment(sketch, "E242.bottom", {"start": v(84, 1.72) * mm, "end": v(85, 1.72) * mm});
            skLineSegment(sketch, "E242.top", {"start": v(84, -1.28) * mm, "end": v(85, -1.28) * mm});
            skLineSegment(sketch, "E242.left", {"start": v(84, 1.72) * mm, "end": v(84, -1.28) * mm});
            skLineSegment(sketch, "E242.right", {"start": v(85, 1.72) * mm, "end": v(85, -1.28) * mm});
            skPoint(sketch, "E242.middle", {"position": v(84.5, 0.22) * mm});
            skCircle(sketch, "E243", {"center": v(19.62, 10.5) * mm, "radius": 1.5 * mm});
            skCircle(sketch, "E244.1.0", {"center": v(-19.62, -10.5) * mm, "radius": 1.5 * mm});
            skSolve(sketch);
        }
        {
            var Q0;
            Q0=makeQuery(id+"F3.imprint","IMPRINT",FACE,{"disambiguationData":[TD([[makeQuery(id+"F3.imprint","IMPRINT",EDGE,{"derivedFrom":sQuery(id+"F3.wireOp",EDGE,"E44")}),-1.0]])]});
            extrude(context, id + "F4", {"entities" : qUnion([Q0]), "endBound" : BoundingType.SYMMETRIC, "depth" : 25 * mm});
        }
        {
            var Q0;
            Q0=makeQuery(id+"F4.opExtrude","SWEPT_BODY",BODY,{"disambiguationData":[OSD([sQuery(id+"F3.wireOp",EDGE,"E44"),sQuery(id+"F3.wireOp",EDGE,"E45"),sQuery(id+"F3.wireOp",EDGE,"E46"),sQuery(id+"F3.wireOp",EDGE,"E47"),sQuery(id+"F3.wireOp",EDGE,"E49.bottom"),sQuery(id+"F3.wireOp",EDGE,"E49.top"),sQuery(id+"F3.wireOp",EDGE,"E50.filletArc"),sQuery(id+"F3.wireOp",EDGE,"E51.filletArc"),sQuery(id+"F3.wireOp",EDGE,"E52.filletArc"),sQuery(id+"F3.wireOp",EDGE,"E53.filletArc"),sQuery(id+"F3.wireOp",EDGE,"E55.bottom"),sQuery(id+"F3.wireOp",EDGE,"E55.top"),sQuery(id+"F3.wireOp",EDGE,"E55.left"),sQuery(id+"F3.wireOp",EDGE,"E55.right"),sQuery(id+"F3.wireOp",EDGE,"E57"),sQuery(id+"F3.wireOp",EDGE,"E59"),sQuery(id+"F3.wireOp",EDGE,"E61"),sQuery(id+"F3.wireOp",EDGE,"E64.bottom"),sQuery(id+"F3.wireOp",EDGE,"E64.top"),sQuery(id+"F3.wireOp",EDGE,"E65.filletArc"),sQuery(id+"F3.wireOp",EDGE,"E66.filletArc"),sQuery(id+"F3.wireOp",EDGE,"E67.filletArc"),sQuery(id+"F3.wireOp",EDGE,"E68.filletArc"),sQuery(id+"F3.wireOp",EDGE,"E70.bottom"),sQuery(id+"F3.wireOp",EDGE,"E70.top"),sQuery(id+"F3.wireOp",EDGE,"E70.left"),sQuery(id+"F3.wireOp",EDGE,"E70.right"),sQuery(id+"F3.wireOp",EDGE,"E71"),sQuery(id+"F3.wireOp",EDGE,"E72"),sQuery(id+"F3.wireOp",EDGE,"E74"),sQuery(id+"F3.wireOp",EDGE,"E76"),sQuery(id+"F3.wireOp",EDGE,"E77"),sQuery(id+"F3.wireOp",EDGE,"E78"),sQuery(id+"F3.wireOp",EDGE,"E79.left"),sQuery(id+"F3.wireOp",EDGE,"E79.right"),sQuery(id+"F3.wireOp",EDGE,"E80.left"),sQuery(id+"F3.wireOp",EDGE,"E80.right"),sQuery(id+"F3.wireOp",EDGE,"E81"),sQuery(id+"F3.wireOp",EDGE,"E82"),sQuery(id+"F3.wireOp",EDGE,"E83.bottom"),sQuery(id+"F3.wireOp",EDGE,"E83.top"),sQuery(id+"F3.wireOp",EDGE,"E83.left"),sQuery(id+"F3.wireOp",EDGE,"E83.right"),sQuery(id+"F3.wireOp",EDGE,"E89.bottom"),sQuery(id+"F3.wireOp",EDGE,"E89.top"),sQuery(id+"F3.wireOp",EDGE,"E90.filletArc"),sQuery(id+"F3.wireOp",EDGE,"E91.filletArc"),sQuery(id+"F3.wireOp",EDGE,"E92.filletArc"),sQuery(id+"F3.wireOp",EDGE,"E93.filletArc"),sQuery(id+"F3.wireOp",EDGE,"E94.MirrorCS"),sQuery(id+"F3.wireOp",EDGE,"E95.MirrorCS"),sQuery(id+"F3.wireOp",EDGE,"E96.MirrorCS"),sQuery(id+"F3.wireOp",EDGE,"E99.MirrorCS"),sQuery(id+"F3.wireOp",EDGE,"E101.MirrorCS"),sQuery(id+"F3.wireOp",EDGE,"E103.MirrorCS"),sQuery(id+"F3.wireOp",EDGE,"E105.MirrorCS"),sQuery(id+"F3.wireOp",EDGE,"E106.MirrorCS"),sQuery(id+"F3.wireOp",EDGE,"E107.MirrorCS"),sQuery(id+"F3.wireOp",EDGE,"E108.MirrorCS"),sQuery(id+"F3.wireOp",EDGE,"E109.MirrorCS"),sQuery(id+"F3.wireOp",EDGE,"E110.MirrorCS"),sQuery(id+"F3.wireOp",EDGE,"E113.MirrorC"),sQuery(id+"F3.wireOp",EDGE,"E114.MirrorC"),sQuery(id+"F3.wireOp",EDGE,"E118.MirrorCS"),sQuery(id+"F3.wireOp",EDGE,"E119.MirrorC"),sQuery(id+"F3.wireOp",EDGE,"E120.MirrorC"),sQuery(id+"F3.wireOp",EDGE,"E121.MirrorC"),sQuery(id+"F3.wireOp",EDGE,"E123.MirrorCS"),sQuery(id+"F3.wireOp",EDGE,"E124.MirrorCS"),sQuery(id+"F3.wireOp",EDGE,"E125.MirrorCS"),sQuery(id+"F3.wireOp",EDGE,"E130.MirrorCS"),sQuery(id+"F3.wireOp",EDGE,"E132.MirrorCS"),sQuery(id+"F3.wireOp",EDGE,"E133.MirrorCS"),sQuery(id+"F3.wireOp",EDGE,"E134.MirrorCS"),sQuery(id+"F3.wireOp",EDGE,"E135.MirrorCS"),sQuery(id+"F3.wireOp",EDGE,"E136.MirrorCS"),sQuery(id+"F3.wireOp",EDGE,"E138"),sQuery(id+"F3.wireOp",EDGE,"E140"),sQuery(id+"F3.wireOp",EDGE,"E141"),sQuery(id+"F3.wireOp",EDGE,"E142"),sQuery(id+"F3.wireOp",EDGE,"E143.filletArc"),sQuery(id+"F3.wireOp",EDGE,"E144.filletArc"),sQuery(id+"F3.wireOp",EDGE,"E145.filletArc"),sQuery(id+"F3.wireOp",EDGE,"E146.filletArc"),sQuery(id+"F3.wireOp",EDGE,"E147"),sQuery(id+"F3.wireOp",EDGE,"E149"),sQuery(id+"F3.wireOp",EDGE,"E150"),sQuery(id+"F3.wireOp",EDGE,"E151"),sQuery(id+"F3.wireOp",EDGE,"E154.MirrorCS"),sQuery(id+"F3.wireOp",EDGE,"E155.MirrorCS"),sQuery(id+"F3.wireOp",EDGE,"E156.MirrorCS"),sQuery(id+"F3.wireOp",EDGE,"E157.MirrorCS"),sQuery(id+"F3.wireOp",EDGE,"E158.MirrorCS"),sQuery(id+"F3.wireOp",EDGE,"E159.MirrorCS"),sQuery(id+"F3.wireOp",EDGE,"E160.MirrorCS"),sQuery(id+"F3.wireOp",EDGE,"E161.MirrorCS"),sQuery(id+"F3.wireOp",EDGE,"E162.MirrorCS"),sQuery(id+"F3.wireOp",EDGE,"E163.MirrorCS"),sQuery(id+"F3.wireOp",EDGE,"E165"),sQuery(id+"F3.wireOp",EDGE,"E169"),sQuery(id+"F3.wireOp",EDGE,"E170"),sQuery(id+"F3.wireOp",EDGE,"E171"),sQuery(id+"F3.wireOp",EDGE,"E175.MirrorCS"),sQuery(id+"F3.wireOp",EDGE,"E176.MirrorCS"),sQuery(id+"F3.wireOp",EDGE,"E177.MirrorCS"),sQuery(id+"F3.wireOp",EDGE,"E178.MirrorCS"),sQuery(id+"F3.wireOp",EDGE,"E180.MirrorCS"),sQuery(id+"F3.wireOp",EDGE,"E181.MirrorCS"),sQuery(id+"F3.wireOp",EDGE,"E183.MirrorCS"),sQuery(id+"F3.wireOp",EDGE,"E184.MirrorCS"),sQuery(id+"F3.wireOp",EDGE,"E188.MirrorC"),sQuery(id+"F3.wireOp",EDGE,"E189"),sQuery(id+"F3.wireOp",EDGE,"E190"),sQuery(id+"F3.wireOp",EDGE,"E191"),sQuery(id+"F3.wireOp",EDGE,"E192"),sQuery(id+"F3.wireOp",EDGE,"E193"),sQuery(id+"F3.wireOp",EDGE,"E196"),sQuery(id+"F3.wireOp",EDGE,"E197"),sQuery(id+"F3.wireOp",EDGE,"E198"),sQuery(id+"F3.wireOp",EDGE,"E199"),sQuery(id+"F3.wireOp",EDGE,"E202.MirrorCS"),sQuery(id+"F3.wireOp",EDGE,"E203.MirrorCS"),sQuery(id+"F3.wireOp",EDGE,"E207.MirrorCS"),sQuery(id+"F3.wireOp",EDGE,"E209.MirrorCS"),sQuery(id+"F3.wireOp",EDGE,"E211.MirrorCS"),sQuery(id+"F3.wireOp",EDGE,"E212.MirrorCS"),sQuery(id+"F3.wireOp",EDGE,"E213.MirrorCS"),sQuery(id+"F3.wireOp",EDGE,"E215"),sQuery(id+"F3.wireOp",EDGE,"E217"),sQuery(id+"F3.wireOp",EDGE,"E218"),sQuery(id+"F3.wireOp",EDGE,"E219"),sQuery(id+"F3.wireOp",EDGE,"E222"),sQuery(id+"F3.wireOp",EDGE,"E223"),sQuery(id+"F3.wireOp",EDGE,"E224"),sQuery(id+"F3.wireOp",EDGE,"E225"),sQuery(id+"F3.wireOp",EDGE,"E228.MirrorCS"),sQuery(id+"F3.wireOp",EDGE,"E229.MirrorCS"),sQuery(id+"F3.wireOp",EDGE,"E233.MirrorCS"),sQuery(id+"F3.wireOp",EDGE,"E235.MirrorCS"),sQuery(id+"F3.wireOp",EDGE,"E237.MirrorCS"),sQuery(id+"F3.wireOp",EDGE,"E238.MirrorCS"),sQuery(id+"F3.wireOp",EDGE,"E239.MirrorCS")])]});
            var Q1;
            Q1=makeQuery(id+"F2.opExtrude","SWEPT_BODY",BODY,{"disambiguationData":[OSD([sQuery(id+"F1.wireOp",EDGE,"E30"),sQuery(id+"F1.wireOp",EDGE,"E32"),sQuery(id+"F1.wireOp",EDGE,"E34"),sQuery(id+"F1.wireOp",EDGE,"E35.0"),sQuery(id+"F1.wireOp",EDGE,"E35.1"),sQuery(id+"F1.wireOp",EDGE,"E35.2"),sQuery(id+"F1.wireOp",EDGE,"E36"),sQuery(id+"F1.wireOp",EDGE,"E37.MirrorCS"),sQuery(id+"F1.wireOp",EDGE,"E38.MirrorCS"),sQuery(id+"F1.wireOp",EDGE,"E39.MirrorCS"),sQuery(id+"F1.wireOp",EDGE,"E40.MirrorCS"),sQuery(id+"F1.wireOp",EDGE,"E41.MirrorCS"),sQuery(id+"F1.wireOp",EDGE,"E42.MirrorCS"),sQuery(id+"F1.wireOp",EDGE,"E43.MirrorCS")])]});
            booleanBodies(context, id + "F5", {"operationType" : BooleanOperationType.INTERSECTION, "tools" : qUnion([Q0, Q1])});
        }
    });
